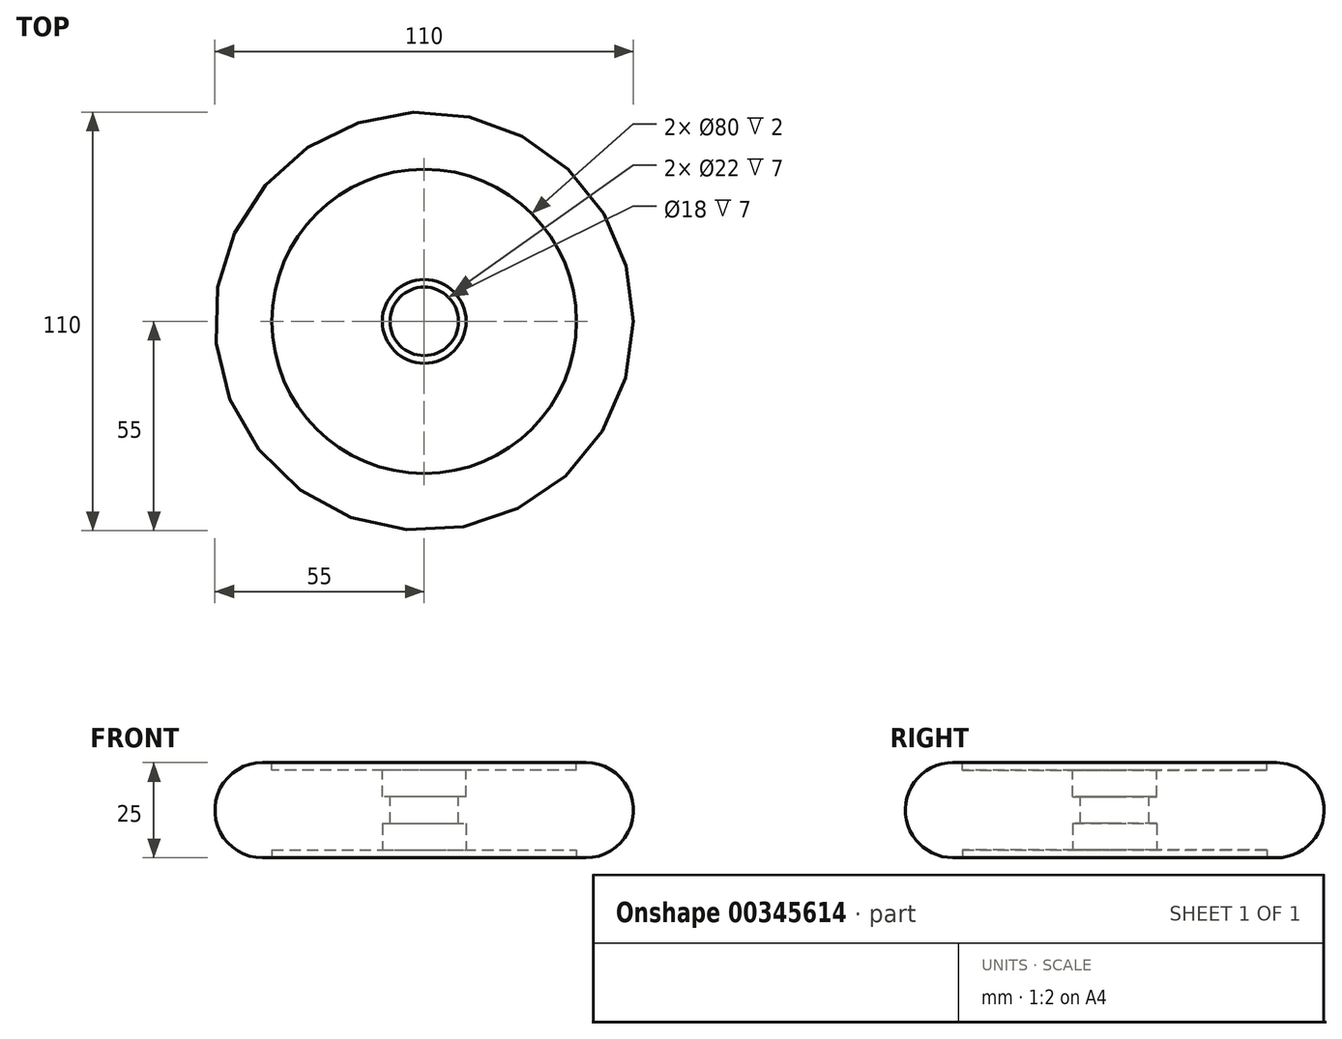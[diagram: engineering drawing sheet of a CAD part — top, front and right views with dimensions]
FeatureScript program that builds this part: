
annotation { "Feature Type Name" : "Feature", "Feature Type Description" : "" }
export const myFeature = defineFeature(function(context is Context, id is Id, definition is map)
    precondition{}
    {
        {
            var Q0;
            Q0=qCreatedBy(makeId("Top.planeOp"),FACE);
            var sketch = newSketch(context, id + "F0", { "sketchPlane" : qUnion([Q0])});
            skCircle(sketch, "E0", {"center": v(0, 0) * mm, "radius": 55 * mm});
            skSolve(sketch);
        }
        {
            var Q0;
            Q0=makeQuery(id+"F0.imprint","IMPRINT",FACE,{"disambiguationData":[TD([[makeQuery(id+"F0.imprint","IMPRINT",EDGE,{"derivedFrom":sQuery(id+"F0.wireOp",EDGE,"E0")}),1.0]])]});
            extrude(context, id + "F1", {"entities" : qUnion([Q0]), "depth" : 25 * mm});
        }
        {
            var Q0;
            Q0=makeQuery(id+"F1.opExtrude","CAP_FACE",FACE,{"disambiguationData":[OSD([sQuery(id+"F0.wireOp",EDGE,"E0")])],"isStart":false});
            var sketch = newSketch(context, id + "F2", { "sketchPlane" : qUnion([Q0])});
            skCircle(sketch, "E1", {"center": v(0, 0) * mm, "radius": 40 * mm});
            skSolve(sketch);
        }
        {
            var Q0;
            Q0 = qSketchRegion(id + "F2", true);
            extrude(context, id + "F3", {"entities" : qUnion([Q0]), "operationType" : NewBodyOperationType.REMOVE, "oppositeDirection" : true, "depth" : 2 * mm});
        }
        {
            var Q0;
            Q0=makeQuery(id+"F3.boolean.opBoolean","COPY",FACE,{"derivedFrom":makeQuery(id+"F3.opExtrude","CAP_FACE",FACE,{"disambiguationData":[OSD([sQuery(id+"F2.wireOp",EDGE,"E1")])],"isStart":false})});
            var sketch = newSketch(context, id + "F4", { "sketchPlane" : qUnion([Q0])});
            skCircle(sketch, "E2", {"center": v(0, 0) * mm, "radius": 11 * mm});
            skSolve(sketch);
        }
        {
            var Q0;
            Q0=makeQuery(id+"F4.imprint","IMPRINT",FACE,{"disambiguationData":[TD([[makeQuery(id+"F4.imprint","IMPRINT",EDGE,{"derivedFrom":sQuery(id+"F4.wireOp",EDGE,"E2")}),1.0]])]});
            extrude(context, id + "F5", {"entities" : qUnion([Q0]), "operationType" : NewBodyOperationType.REMOVE, "oppositeDirection" : true, "depth" : 7 * mm});
        }
        {
            var Q0;
            Q0=makeQuery(id+"F1.opExtrude","CAP_FACE",FACE,{"disambiguationData":[OSD([sQuery(id+"F0.wireOp",EDGE,"E0")])],"isStart":true});
            var sketch = newSketch(context, id + "F6", { "sketchPlane" : qUnion([Q0])});
            skCircle(sketch, "E3", {"center": v(0, 0) * mm, "radius": 40 * mm});
            skSolve(sketch);
        }
        {
            var Q0;
            Q0=makeQuery(id+"F6.imprint","IMPRINT",FACE,{"disambiguationData":[TD([[makeQuery(id+"F6.imprint","IMPRINT",EDGE,{"derivedFrom":sQuery(id+"F6.wireOp",EDGE,"E3")}),1.0]])]});
            extrude(context, id + "F7", {"entities" : qUnion([Q0]), "operationType" : NewBodyOperationType.REMOVE, "oppositeDirection" : true, "depth" : 2 * mm});
        }
        {
            var Q0;
            Q0=makeQuery(id+"F7.boolean.opBoolean","COPY",FACE,{"derivedFrom":makeQuery(id+"F7.opExtrude","CAP_FACE",FACE,{"disambiguationData":[OSD([sQuery(id+"F6.wireOp",EDGE,"E3")])],"isStart":false})});
            var sketch = newSketch(context, id + "F8", { "sketchPlane" : qUnion([Q0])});
            skCircle(sketch, "E4", {"center": v(0, 0) * mm, "radius": 11 * mm});
            skSolve(sketch);
        }
        {
            var Q0;
            Q0=makeQuery(id+"F8.imprint","IMPRINT",FACE,{"disambiguationData":[TD([[makeQuery(id+"F8.imprint","IMPRINT",EDGE,{"derivedFrom":sQuery(id+"F8.wireOp",EDGE,"E4")}),1.0]])]});
            extrude(context, id + "F9", {"entities" : qUnion([Q0]), "operationType" : NewBodyOperationType.REMOVE, "oppositeDirection" : true, "depth" : 7 * mm});
        }
        {
            var Q0;
            Q0=makeQuery(id+"F5.boolean.opBoolean","COPY",FACE,{"derivedFrom":makeQuery(id+"F5.opExtrude","CAP_FACE",FACE,{"disambiguationData":[OSD([sQuery(id+"F4.wireOp",EDGE,"E2")])],"isStart":false})});
            var sketch = newSketch(context, id + "F10", { "sketchPlane" : qUnion([Q0])});
            skCircle(sketch, "E5", {"center": v(0, 0) * mm, "radius": 9 * mm});
            skSolve(sketch);
        }
        {
            var Q0;
            Q0=makeQuery(id+"F10.imprint","IMPRINT",FACE,{"disambiguationData":[TD([[makeQuery(id+"F10.imprint","IMPRINT",EDGE,{"derivedFrom":sQuery(id+"F10.wireOp",EDGE,"E5")}),1.0]])]});
            extrude(context, id + "F11", {"entities" : qUnion([Q0]), "operationType" : NewBodyOperationType.REMOVE, "oppositeDirection" : true, "depth" : 25 * mm});
        }
        {
            var Q0;
            Q0=makeQuery(id+"F1.opExtrude","CAP_EDGE",EDGE,{"disambiguationData":[OSD([sQuery(id+"F0.wireOp",EDGE,"E0")])],"isStart":false});
            var Q1;
            Q1=makeQuery(id+"F1.opExtrude","CAP_EDGE",EDGE,{"disambiguationData":[OSD([sQuery(id+"F0.wireOp",EDGE,"E0")])],"isStart":true});
            fillet(context, id + "F12", {"entities" : qUnion([Q0, Q1]), "radius" : 12.5 * mm, "tangentPropagation" : true, "allowEdgeOverflow" : false});
        }
    });
